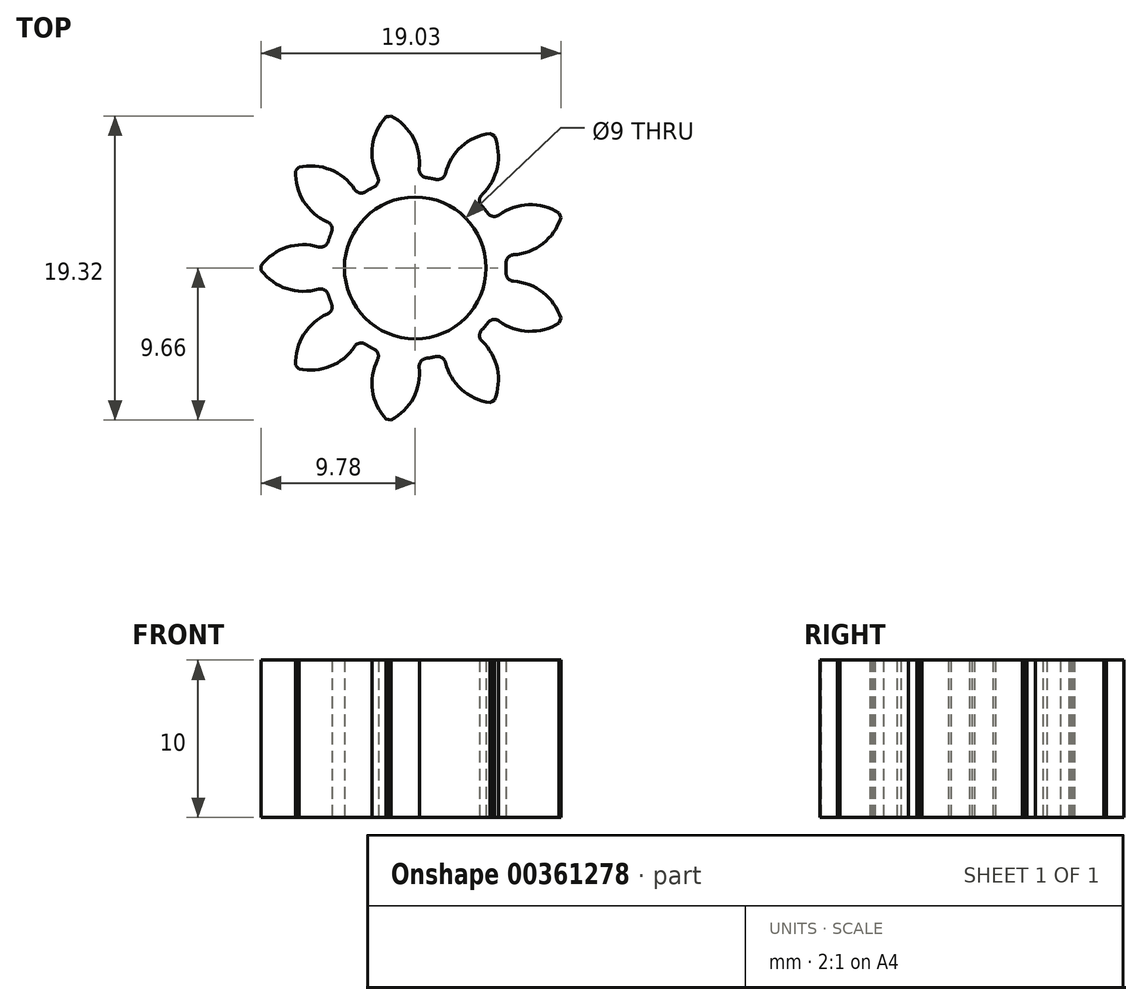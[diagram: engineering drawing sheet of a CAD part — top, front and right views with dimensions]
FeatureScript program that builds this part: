
annotation { "Feature Type Name" : "Feature", "Feature Type Description" : "" }
export const myFeature = defineFeature(function(context is Context, id is Id, definition is map)
    precondition{}
    {
        {
            var Q0;
            Q0=qCreatedBy(makeId("Top.planeOp"),FACE);
            var sketch = newSketch(context, id + "F0", { "sketchPlane" : qUnion([Q0])});
            skCircle(sketch, "E0", {"center": v(0, 0) * mm, "radius": 8 * mm, "construction": true});
            skArc(sketch, "E1", {"start": v(1.86, -9.6) * mm, "mid": v(-1.7, 9.63) * mm, "end": v(1.54, -9.66) * mm, "construction": true});
            skArc(sketch, "E2", {"start": v(-2.62, 5.15) * mm, "mid": v(-2.75, 5.08) * mm, "end": v(-2.9, 5) * mm});
            skLineSegment(sketch, "E3", {"start": v(0, 0) * mm, "end": v(0, 16) * mm, "construction": true});
            skCircle(sketch, "E4", {"center": v(0, 16) * mm, "radius": 9.78 * mm, "construction": true});
            skCircle(sketch, "E5", {"center": v(0, 16) * mm, "radius": 8 * mm, "construction": true});
            skCircle(sketch, "E6", {"center": v(0, 16) * mm, "radius": 5.78 * mm, "construction": true});
            skLineSegment(sketch, "E7", {"start": v(0, 8) * mm, "end": v(-27.15, 8) * mm, "construction": true});
            skLineSegment(sketch, "E8", {"start": v(0, 8) * mm, "end": v(-27.15, -1.88) * mm, "construction": true});
            skLineSegment(sketch, "E9", {"start": v(0, 8) * mm, "end": v(27.4, 17.17) * mm, "construction": true});
            skCircle(sketch, "E10", {"center": v(0, 16) * mm, "radius": 7.59 * mm, "construction": true});
            skCircle(sketch, "E11", {"center": v(0, 16) * mm, "radius": 8.93 * mm, "construction": true});
            skLineSegment(sketch, "E12", {"start": v(-3.3, 6.8) * mm, "end": v(-1.66, 2.28) * mm, "construction": true});
            skLineSegment(sketch, "E13", {"start": v(-1.97, 7.28) * mm, "end": v(-0.22, 2.5) * mm, "construction": true});
            skLineSegment(sketch, "E14", {"start": v(0, 8) * mm, "end": v(1.86, 2.9) * mm, "construction": true});
            skLineSegment(sketch, "E15", {"start": v(2.4, 8.8) * mm, "end": v(4.64, 2.67) * mm, "construction": true});
            skLineSegment(sketch, "E16", {"start": v(0, 0) * mm, "end": v(-3.3, 6.8) * mm, "construction": true});
            skLineSegment(sketch, "E17", {"start": v(0, 0) * mm, "end": v(-1.97, 7.28) * mm, "construction": true});
            skLineSegment(sketch, "E18", {"start": v(0, 0) * mm, "end": v(2.4, 8.8) * mm, "construction": true});
            skLineSegment(sketch, "E19", {"start": v(0, 8) * mm, "end": v(0.44, 2.91) * mm, "construction": true});
            skLineSegment(sketch, "E20", {"start": v(0.19, 7.8) * mm, "end": v(0.3, 6.61) * mm, "construction": true});
            skLineSegment(sketch, "E21", {"start": v(0, 8) * mm, "end": v(-0.42, 3.94) * mm, "construction": true});
            skLineSegment(sketch, "E22", {"start": v(0.3, 6.61) * mm, "end": v(0.15, 5.2) * mm, "construction": true});
            skLineSegment(sketch, "E23", {"start": v(0, 8) * mm, "end": v(4.64, 1.45) * mm, "construction": true});
            skLineSegment(sketch, "E24", {"start": v(0.23, 7.38) * mm, "end": v(-0.08, 8.2) * mm, "construction": true});
            skLineSegment(sketch, "E25", {"start": v(-0.22, 8.42) * mm, "end": v(3.11, 3.7) * mm, "construction": true});
            skArc(sketch, "E26", {"start": v(0.26, 6.29) * mm, "mid": v(-0.12, 8.25) * mm, "end": v(-1.54, 9.66) * mm});
            skPoint(sketch, "E26.second.point", {"position": v(0.25, 7.07) * mm});
            skLineSegment(sketch, "E27", {"start": v(0, 0) * mm, "end": v(4.38, 12.05) * mm, "construction": true});
            skLineSegment(sketch, "E28", {"start": v(0, 0) * mm, "end": v(-2.24, 12.69) * mm, "construction": true});
            skLineSegment(sketch, "E29", {"start": v(0, 0) * mm, "end": v(-4.52, 12.43) * mm, "construction": true});
            skLineSegment(sketch, "E30", {"start": v(-1.54, 9.66) * mm, "end": v(-1.7, 9.63) * mm});
            skLineSegment(sketch, "E31", {"start": v(0, 0) * mm, "end": v(2.57, 14.55) * mm, "construction": true});
            skPoint(sketch, "E32.visualSharp", {"position": v(0.16, 5.78) * mm});
            skLineSegment(sketch, "E32.filletArc", {"start": v(0.16, 5.78) * mm, "end": v(0.16, 5.78) * mm});
            skLineSegment(sketch, "E33.MirrorCS", {"start": v(-1.86, 9.6) * mm, "end": v(-1.7, 9.63) * mm});
            skLineSegment(sketch, "E34.MirrorCS", {"start": v(-2.13, 5.37) * mm, "end": v(-2.13, 5.37) * mm});
            skArc(sketch, "E35.MirrorCS", {"start": v(-2.4, 5.82) * mm, "mid": v(-2.7, 7.8) * mm, "end": v(-1.86, 9.6) * mm});
            skCircle(sketch, "E36", {"center": v(0, 0) * mm, "radius": 4.5 * mm});
            skArc(sketch, "E37.filletArc", {"start": v(0.26, 6.29) * mm, "mid": v(0.36, 5.92) * mm, "end": v(0.7, 5.74) * mm});
            skArc(sketch, "E38.filletArc", {"start": v(-2.62, 5.15) * mm, "mid": v(-2.37, 5.44) * mm, "end": v(-2.4, 5.82) * mm});
            skArc(sketch, "E39.trimOffspring", {"start": v(1, 5.7) * mm, "mid": v(0.85, 5.72) * mm, "end": v(0.7, 5.74) * mm});
            skLineSegment(sketch, "E40", {"start": v(0, 0) * mm, "end": v(-6.85, 11.86) * mm, "construction": true});
            skLineSegment(sketch, "E41.1.0", {"start": v(-7.39, 6.41) * mm, "end": v(-7.5, 6.29) * mm});
            skLineSegment(sketch, "E41.1.1", {"start": v(-7.6, 6.16) * mm, "end": v(-7.5, 6.29) * mm});
            skArc(sketch, "E41.1.2", {"start": v(-3.85, 4.98) * mm, "mid": v(-5.4, 6.24) * mm, "end": v(-7.39, 6.41) * mm});
            skArc(sketch, "E41.1.3", {"start": v(-5.57, 2.92) * mm, "mid": v(-7.08, 4.23) * mm, "end": v(-7.6, 6.16) * mm});
            skArc(sketch, "E41.1.4", {"start": v(-3.85, 4.98) * mm, "mid": v(-3.53, 4.77) * mm, "end": v(-3.16, 4.84) * mm});
            skArc(sketch, "E41.1.5", {"start": v(-2.9, 5) * mm, "mid": v(-3.02, 4.93) * mm, "end": v(-3.16, 4.84) * mm});
            skArc(sketch, "E41.1.6", {"start": v(-5.32, 2.27) * mm, "mid": v(-5.31, 2.65) * mm, "end": v(-5.57, 2.92) * mm});
            skArc(sketch, "E41.1.7", {"start": v(-5.32, 2.27) * mm, "mid": v(-5.38, 2.12) * mm, "end": v(-5.43, 1.98) * mm});
            skLineSegment(sketch, "E41.2.0", {"start": v(-9.78, 0.16) * mm, "end": v(-9.78, 0) * mm});
            skLineSegment(sketch, "E41.2.1", {"start": v(-9.78, -0.16) * mm, "end": v(-9.78, 0) * mm});
            skArc(sketch, "E41.2.2", {"start": v(-6.15, 1.35) * mm, "mid": v(-8.15, 1.31) * mm, "end": v(-9.78, 0.16) * mm});
            skArc(sketch, "E41.2.3", {"start": v(-6.15, -1.35) * mm, "mid": v(-8.15, -1.31) * mm, "end": v(-9.78, -0.16) * mm});
            skArc(sketch, "E41.2.4", {"start": v(-6.15, 1.35) * mm, "mid": v(-5.77, 1.39) * mm, "end": v(-5.53, 1.68) * mm});
            skArc(sketch, "E41.2.5", {"start": v(-5.43, 1.98) * mm, "mid": v(-5.48, 1.83) * mm, "end": v(-5.53, 1.68) * mm});
            skArc(sketch, "E41.2.6", {"start": v(-5.53, -1.68) * mm, "mid": v(-5.77, -1.39) * mm, "end": v(-6.15, -1.35) * mm});
            skArc(sketch, "E41.2.7", {"start": v(-5.53, -1.68) * mm, "mid": v(-5.48, -1.83) * mm, "end": v(-5.43, -1.98) * mm});
            skLineSegment(sketch, "E41.3.0", {"start": v(-7.6, -6.16) * mm, "end": v(-7.5, -6.29) * mm});
            skLineSegment(sketch, "E41.3.1", {"start": v(-7.39, -6.41) * mm, "end": v(-7.5, -6.29) * mm});
            skArc(sketch, "E41.3.2", {"start": v(-5.57, -2.92) * mm, "mid": v(-7.08, -4.23) * mm, "end": v(-7.6, -6.16) * mm});
            skArc(sketch, "E41.3.3", {"start": v(-3.85, -4.98) * mm, "mid": v(-5.4, -6.24) * mm, "end": v(-7.39, -6.41) * mm});
            skArc(sketch, "E41.3.4", {"start": v(-5.57, -2.92) * mm, "mid": v(-5.31, -2.65) * mm, "end": v(-5.32, -2.27) * mm});
            skArc(sketch, "E41.3.5", {"start": v(-5.43, -1.98) * mm, "mid": v(-5.38, -2.12) * mm, "end": v(-5.32, -2.27) * mm});
            skArc(sketch, "E41.3.6", {"start": v(-3.16, -4.84) * mm, "mid": v(-3.53, -4.77) * mm, "end": v(-3.85, -4.98) * mm});
            skArc(sketch, "E41.3.7", {"start": v(-3.16, -4.84) * mm, "mid": v(-3.02, -4.93) * mm, "end": v(-2.89, -5) * mm});
            skLineSegment(sketch, "E41.4.0", {"start": v(-1.86, -9.6) * mm, "end": v(-1.7, -9.63) * mm});
            skLineSegment(sketch, "E41.4.1", {"start": v(-1.54, -9.66) * mm, "end": v(-1.7, -9.63) * mm});
            skArc(sketch, "E41.4.2", {"start": v(-2.4, -5.82) * mm, "mid": v(-2.7, -7.8) * mm, "end": v(-1.86, -9.6) * mm});
            skArc(sketch, "E41.4.3", {"start": v(0.26, -6.29) * mm, "mid": v(-0.12, -8.25) * mm, "end": v(-1.54, -9.66) * mm});
            skArc(sketch, "E41.4.4", {"start": v(-2.4, -5.82) * mm, "mid": v(-2.37, -5.44) * mm, "end": v(-2.62, -5.15) * mm});
            skArc(sketch, "E41.4.5", {"start": v(-2.9, -5) * mm, "mid": v(-2.75, -5.08) * mm, "end": v(-2.62, -5.15) * mm});
            skArc(sketch, "E41.4.6", {"start": v(0.7, -5.74) * mm, "mid": v(0.36, -5.92) * mm, "end": v(0.26, -6.29) * mm});
            skArc(sketch, "E41.4.7", {"start": v(0.7, -5.74) * mm, "mid": v(0.85, -5.72) * mm, "end": v(1, -5.7) * mm});
            skLineSegment(sketch, "E41.5.0", {"start": v(4.75, -8.55) * mm, "end": v(4.9, -8.47) * mm});
            skLineSegment(sketch, "E41.5.1", {"start": v(5.03, -8.39) * mm, "end": v(4.9, -8.47) * mm});
            skArc(sketch, "E41.5.2", {"start": v(1.9, -6) * mm, "mid": v(2.93, -7.71) * mm, "end": v(4.75, -8.55) * mm});
            skArc(sketch, "E41.5.3", {"start": v(4.24, -4.65) * mm, "mid": v(5.21, -6.4) * mm, "end": v(5.03, -8.39) * mm});
            skArc(sketch, "E41.5.4", {"start": v(1.9, -6) * mm, "mid": v(1.68, -5.7) * mm, "end": v(1.3, -5.63) * mm});
            skArc(sketch, "E41.5.5", {"start": v(1, -5.7) * mm, "mid": v(1.16, -5.66) * mm, "end": v(1.3, -5.63) * mm});
            skArc(sketch, "E41.5.6", {"start": v(4.22, -3.95) * mm, "mid": v(4.09, -4.3) * mm, "end": v(4.24, -4.65) * mm});
            skArc(sketch, "E41.5.7", {"start": v(4.22, -3.95) * mm, "mid": v(4.33, -3.83) * mm, "end": v(4.43, -3.72) * mm});
            skLineSegment(sketch, "E41.6.0", {"start": v(9.13, -3.5) * mm, "end": v(9.2, -3.35) * mm});
            skLineSegment(sketch, "E41.6.1", {"start": v(9.25, -3.19) * mm, "end": v(9.2, -3.35) * mm});
            skArc(sketch, "E41.6.2", {"start": v(5.32, -3.37) * mm, "mid": v(7.2, -4.02) * mm, "end": v(9.13, -3.5) * mm});
            skArc(sketch, "E41.6.3", {"start": v(6.24, -0.84) * mm, "mid": v(8.1, -1.55) * mm, "end": v(9.25, -3.19) * mm});
            skArc(sketch, "E41.6.4", {"start": v(5.32, -3.37) * mm, "mid": v(4.95, -3.28) * mm, "end": v(4.62, -3.47) * mm});
            skArc(sketch, "E41.6.5", {"start": v(4.43, -3.72) * mm, "mid": v(4.53, -3.6) * mm, "end": v(4.62, -3.47) * mm});
            skArc(sketch, "E41.6.6", {"start": v(5.77, -0.31) * mm, "mid": v(5.9, -0.67) * mm, "end": v(6.24, -0.84) * mm});
            skArc(sketch, "E41.6.7", {"start": v(5.77, -0.31) * mm, "mid": v(5.78, -0.16) * mm, "end": v(5.78, 0) * mm});
            skLineSegment(sketch, "E41.7.0", {"start": v(9.25, 3.19) * mm, "end": v(9.2, 3.35) * mm});
            skLineSegment(sketch, "E41.7.1", {"start": v(9.13, 3.5) * mm, "end": v(9.2, 3.35) * mm});
            skArc(sketch, "E41.7.2", {"start": v(6.24, 0.84) * mm, "mid": v(8.1, 1.55) * mm, "end": v(9.25, 3.19) * mm});
            skArc(sketch, "E41.7.3", {"start": v(5.32, 3.37) * mm, "mid": v(7.2, 4.02) * mm, "end": v(9.13, 3.5) * mm});
            skArc(sketch, "E41.7.4", {"start": v(6.24, 0.84) * mm, "mid": v(5.9, 0.67) * mm, "end": v(5.77, 0.31) * mm});
            skArc(sketch, "E41.7.5", {"start": v(5.78, 0) * mm, "mid": v(5.78, 0.16) * mm, "end": v(5.77, 0.31) * mm});
            skArc(sketch, "E41.7.6", {"start": v(4.62, 3.47) * mm, "mid": v(4.95, 3.28) * mm, "end": v(5.32, 3.37) * mm});
            skArc(sketch, "E41.7.7", {"start": v(4.62, 3.47) * mm, "mid": v(4.53, 3.6) * mm, "end": v(4.43, 3.72) * mm});
            skLineSegment(sketch, "E41.8.0", {"start": v(5.03, 8.39) * mm, "end": v(4.9, 8.47) * mm});
            skLineSegment(sketch, "E41.8.1", {"start": v(4.75, 8.55) * mm, "end": v(4.9, 8.47) * mm});
            skArc(sketch, "E41.8.2", {"start": v(4.24, 4.65) * mm, "mid": v(5.21, 6.4) * mm, "end": v(5.03, 8.39) * mm});
            skArc(sketch, "E41.8.3", {"start": v(1.9, 6) * mm, "mid": v(2.93, 7.71) * mm, "end": v(4.75, 8.55) * mm});
            skArc(sketch, "E41.8.4", {"start": v(4.24, 4.65) * mm, "mid": v(4.09, 4.3) * mm, "end": v(4.22, 3.95) * mm});
            skArc(sketch, "E41.8.5", {"start": v(4.43, 3.72) * mm, "mid": v(4.33, 3.83) * mm, "end": v(4.22, 3.95) * mm});
            skArc(sketch, "E41.8.6", {"start": v(1.3, 5.63) * mm, "mid": v(1.68, 5.7) * mm, "end": v(1.9, 6) * mm});
            skArc(sketch, "E41.8.7", {"start": v(1.3, 5.63) * mm, "mid": v(1.16, 5.66) * mm, "end": v(1, 5.7) * mm});
            skSolve(sketch);
        }
        {
            var Q0;
            Q0=makeQuery(id+"F0.imprint","IMPRINT",FACE,{"disambiguationData":[TD([[makeQuery(id+"F0.imprint","IMPRINT",EDGE,{"derivedFrom":sQuery(id+"F0.wireOp",EDGE,"E26")}),1.0]])]});
            extrude(context, id + "F1", {"entities" : qUnion([Q0]), "depth" : 10 * mm});
        }
    });
